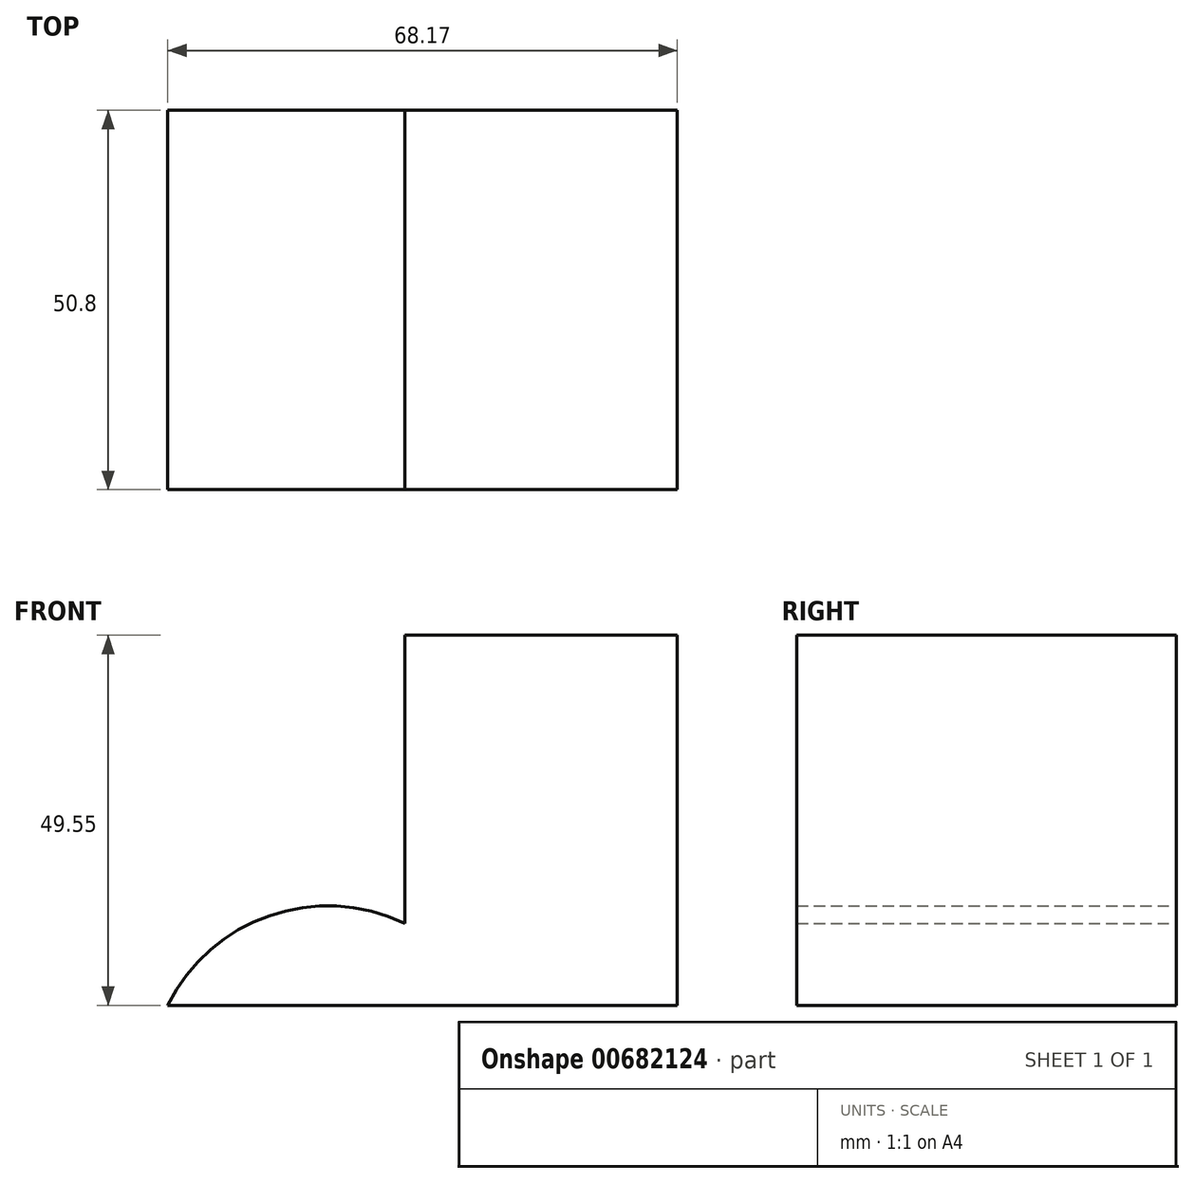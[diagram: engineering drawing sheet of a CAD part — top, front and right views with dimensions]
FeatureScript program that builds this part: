
annotation { "Feature Type Name" : "Feature", "Feature Type Description" : "" }
export const myFeature = defineFeature(function(context is Context, id is Id, definition is map)
    precondition{}
    {
        {
            var Q0;
            Q0=qCreatedBy(makeId("Front.planeOp"),FACE);
            var sketch = newSketch(context, id + "F0", { "sketchPlane" : qUnion([Q0])});
            skLineSegment(sketch, "E0", {"start": v(0, 0) * mm, "end": v(-43.82, 0) * mm});
            skArc(sketch, "E1", {"start": v(-12.13, 10.98) * mm, "mid": v(-30.23, 12) * mm, "end": v(-43.82, 0) * mm});
            skLineSegment(sketch, "E2", {"start": v(-12.13, 10.98) * mm, "end": v(-12.13, 49.55) * mm});
            skLineSegment(sketch, "E3", {"start": v(-12.13, 49.55) * mm, "end": v(21.67, 49.55) * mm});
            skLineSegment(sketch, "E4", {"start": v(0, 0) * mm, "end": v(24.35, 0) * mm});
            skLineSegment(sketch, "E5", {"start": v(24.35, 0) * mm, "end": v(24.35, 49.55) * mm});
            skLineSegment(sketch, "E6", {"start": v(24.35, 49.55) * mm, "end": v(21.67, 49.55) * mm});
            skSolve(sketch);
        }
        {
            var Q0;
            Q0 = qSketchRegion(id + "F0", true);
            extrude(context, id + "F1", {"entities" : qUnion([Q0]), "depth" : 50.8 * mm, "offsetDistance" : 25.4 * mm});
        }
    });
